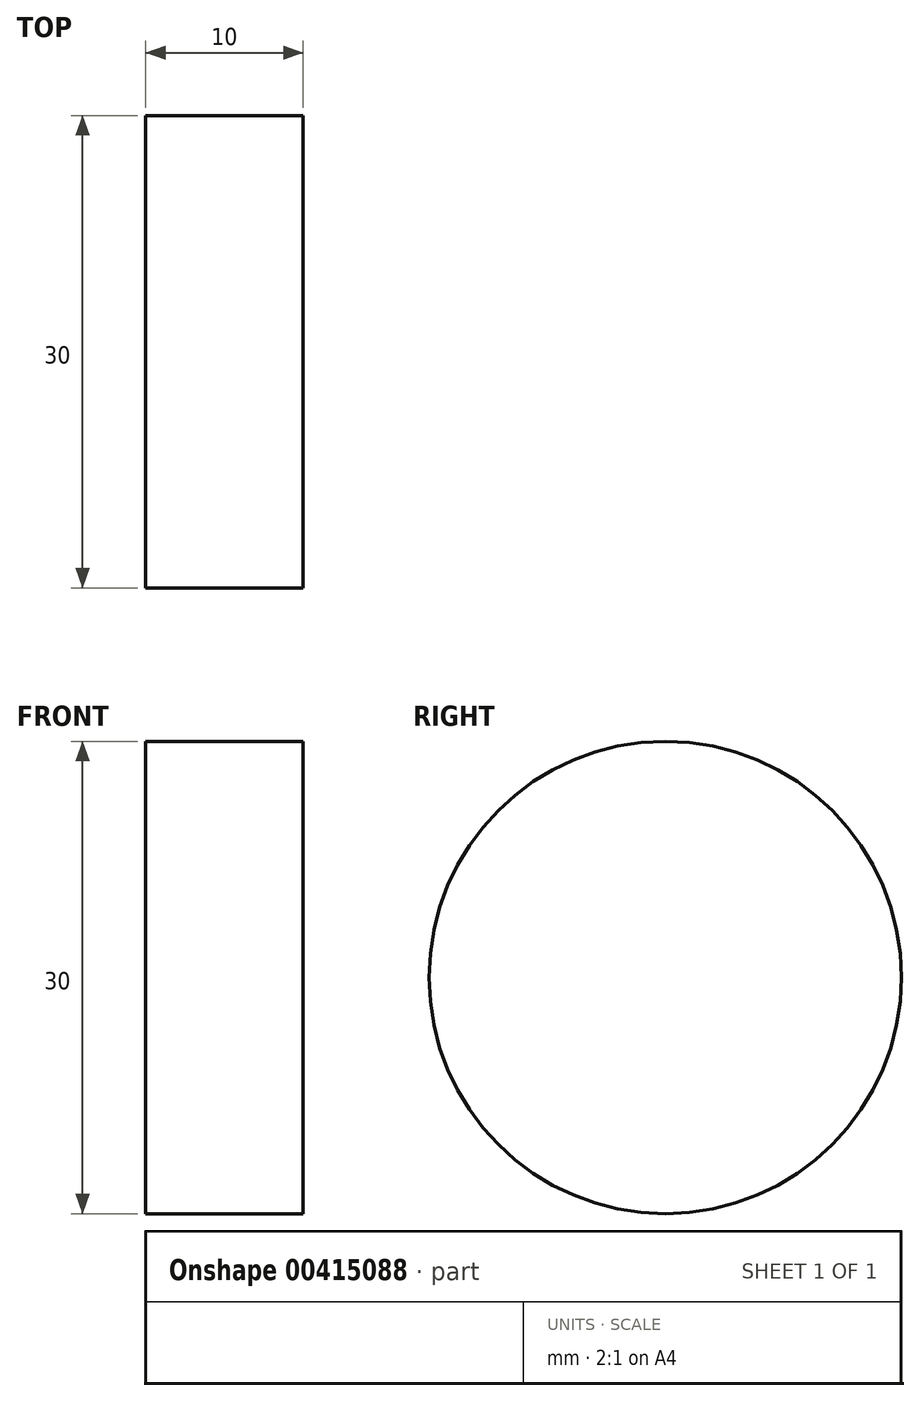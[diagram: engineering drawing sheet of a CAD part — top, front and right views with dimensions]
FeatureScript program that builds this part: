
annotation { "Feature Type Name" : "Feature", "Feature Type Description" : "" }
export const myFeature = defineFeature(function(context is Context, id is Id, definition is map)
    precondition{}
    {
        {
            var Q0;
            Q0=qCreatedBy(makeId("Right.planeOp"),FACE);
            var sketch = newSketch(context, id + "F0", { "sketchPlane" : qUnion([Q0])});
            skCircle(sketch, "E0", {"center": v(0, 0) * mm, "radius": 15 * mm});
            skSolve(sketch);
        }
        {
            var Q0;
            Q0=makeQuery(id+"F0.imprint","IMPRINT",FACE,{"disambiguationData":[TD([[makeQuery(id+"F0.imprint","IMPRINT",EDGE,{"derivedFrom":sQuery(id+"F0.wireOp",EDGE,"E0")}),1.0]])]});
            extrude(context, id + "F1", {"entities" : qUnion([Q0]), "depth" : 10 * mm});
        }
    });
